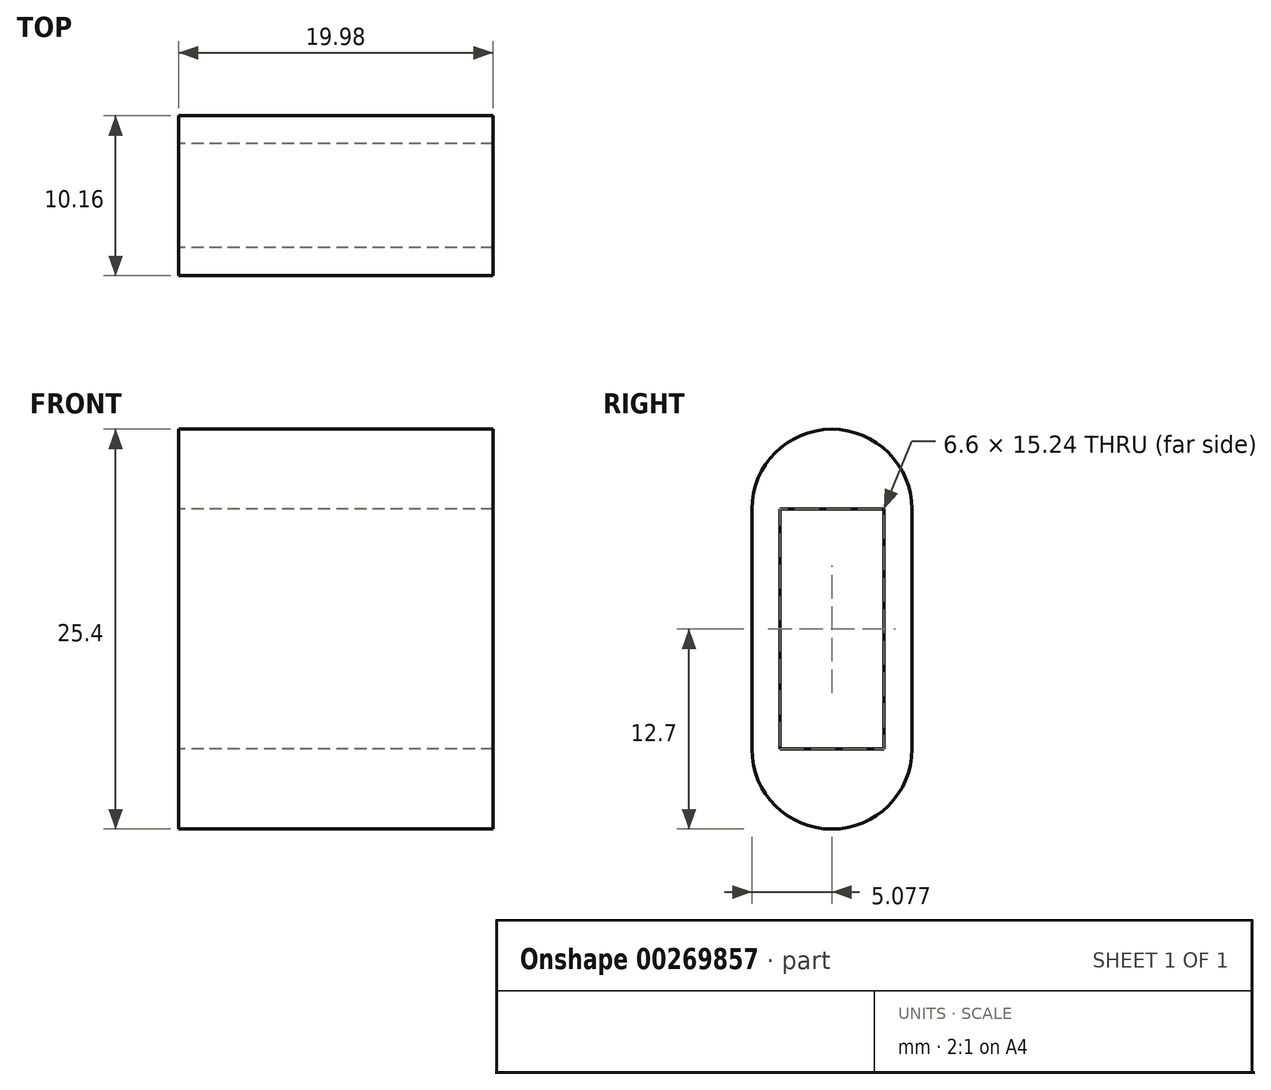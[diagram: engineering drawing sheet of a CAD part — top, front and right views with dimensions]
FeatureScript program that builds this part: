
annotation { "Feature Type Name" : "Feature", "Feature Type Description" : "" }
export const myFeature = defineFeature(function(context is Context, id is Id, definition is map)
    precondition{}
    {
        {
            var Q0;
            Q0=qCreatedBy(makeId("Right.planeOp"),FACE);
            var sketch = newSketch(context, id + "F0", { "sketchPlane" : qUnion([Q0])});
            skLineSegment(sketch, "E0.bottom", {"start": v(1.72, 0) * mm, "end": v(11.88, 0) * mm});
            skLineSegment(sketch, "E0.top", {"start": v(1.72, 25.4) * mm, "end": v(11.88, 25.4) * mm});
            skLineSegment(sketch, "E0.left", {"start": v(1.72, 0) * mm, "end": v(1.72, 25.4) * mm});
            skLineSegment(sketch, "E0.right", {"start": v(11.88, 0) * mm, "end": v(11.88, 25.4) * mm});
            skLineSegment(sketch, "E1.bottom", {"start": v(3.5, 5.08) * mm, "end": v(10.1, 5.08) * mm});
            skLineSegment(sketch, "E1.top", {"start": v(3.5, 20.32) * mm, "end": v(10.1, 20.32) * mm});
            skLineSegment(sketch, "E1.left", {"start": v(3.5, 5.08) * mm, "end": v(3.5, 20.32) * mm});
            skLineSegment(sketch, "E1.right", {"start": v(10.1, 5.08) * mm, "end": v(10.1, 20.32) * mm});
            skSolve(sketch);
        }
        {
            var Q0;
            Q0 = qSketchRegion(id + "F0", true);
            extrude(context, id + "F1", {"entities" : qUnion([Q0]), "depth" : 19.98 * mm});
        }
        {
            var Q0;
            Q0=makeQuery(id+"F1.opExtrude","SWEPT_EDGE",EDGE,{"disambiguationData":[OSD([sQuery(id+"F0.wireOp",EDGE,"E0.top"),sQuery(id+"F0.wireOp",EDGE,"E0.left")])]});
            var Q1;
            Q1=makeQuery(id+"F1.opExtrude","SWEPT_EDGE",EDGE,{"disambiguationData":[OSD([sQuery(id+"F0.wireOp",EDGE,"E0.top"),sQuery(id+"F0.wireOp",EDGE,"E0.right")])]});
            var Q2;
            Q2=makeQuery(id+"F1.opExtrude","SWEPT_EDGE",EDGE,{"disambiguationData":[OSD([sQuery(id+"F0.wireOp",EDGE,"E0.bottom"),sQuery(id+"F0.wireOp",EDGE,"E0.left")])]});
            var Q3;
            Q3=makeQuery(id+"F1.opExtrude","SWEPT_EDGE",EDGE,{"disambiguationData":[OSD([sQuery(id+"F0.wireOp",EDGE,"E0.bottom"),sQuery(id+"F0.wireOp",EDGE,"E0.right")])]});
            fillet(context, id + "F2", {"entities" : qUnion([Q0, Q1, Q2, Q3]), "radius" : 5.08 * mm, "tangentPropagation" : true, "allowEdgeOverflow" : false});
        }
    });
